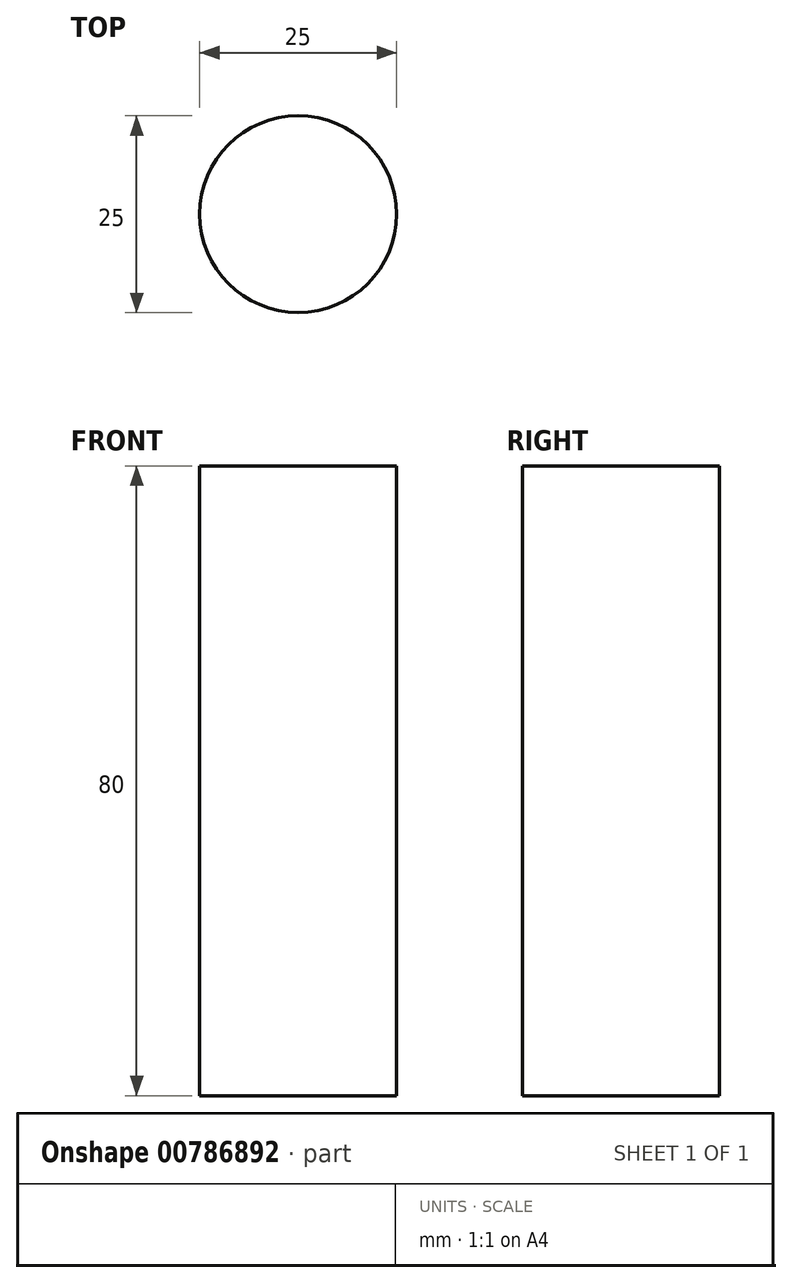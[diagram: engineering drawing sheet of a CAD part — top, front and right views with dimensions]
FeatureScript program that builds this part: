
annotation { "Feature Type Name" : "Feature", "Feature Type Description" : "" }
export const myFeature = defineFeature(function(context is Context, id is Id, definition is map)
    precondition{}
    {
        {
            var Q0;
            Q0=qCreatedBy(makeId("Front.planeOp"),FACE);
            var sketch = newSketch(context, id + "F0", { "sketchPlane" : qUnion([Q0])});
            skLineSegment(sketch, "E0.bottom", {"start": v(-12.5, 40) * mm, "end": v(0, 40) * mm});
            skLineSegment(sketch, "E0.top", {"start": v(-12.5, -40) * mm, "end": v(0, -40) * mm});
            skLineSegment(sketch, "E0.left", {"start": v(-12.5, 40) * mm, "end": v(-12.5, -40) * mm});
            skLineSegment(sketch, "E0.right", {"start": v(0, 40) * mm, "end": v(0, -40) * mm});
            skLineSegment(sketch, "E1", {"start": v(0, 64.22) * mm, "end": v(0, -58.5) * mm, "construction": true});
            skSolve(sketch);
        }
        {
            var Q0;
            Q0=makeQuery(id+"F0.imprint","IMPRINT",FACE,{"disambiguationData":[TD([[makeQuery(id+"F0.imprint","IMPRINT",EDGE,{"derivedFrom":sQuery(id+"F0.wireOp",EDGE,"E0.bottom")}),-1.0]])]});
            var Q1;
            Q1=sQuery(id+"F0.wireOp",EDGE,"E1");
            revolve(context, id + "F1", {"surfaceOperationType" : NewSurfaceOperationType.NEW, "entities" : qUnion([Q0]), "axis" : qUnion([Q1]), "revolveType" : RevolveType.FULL});
        }
    });
